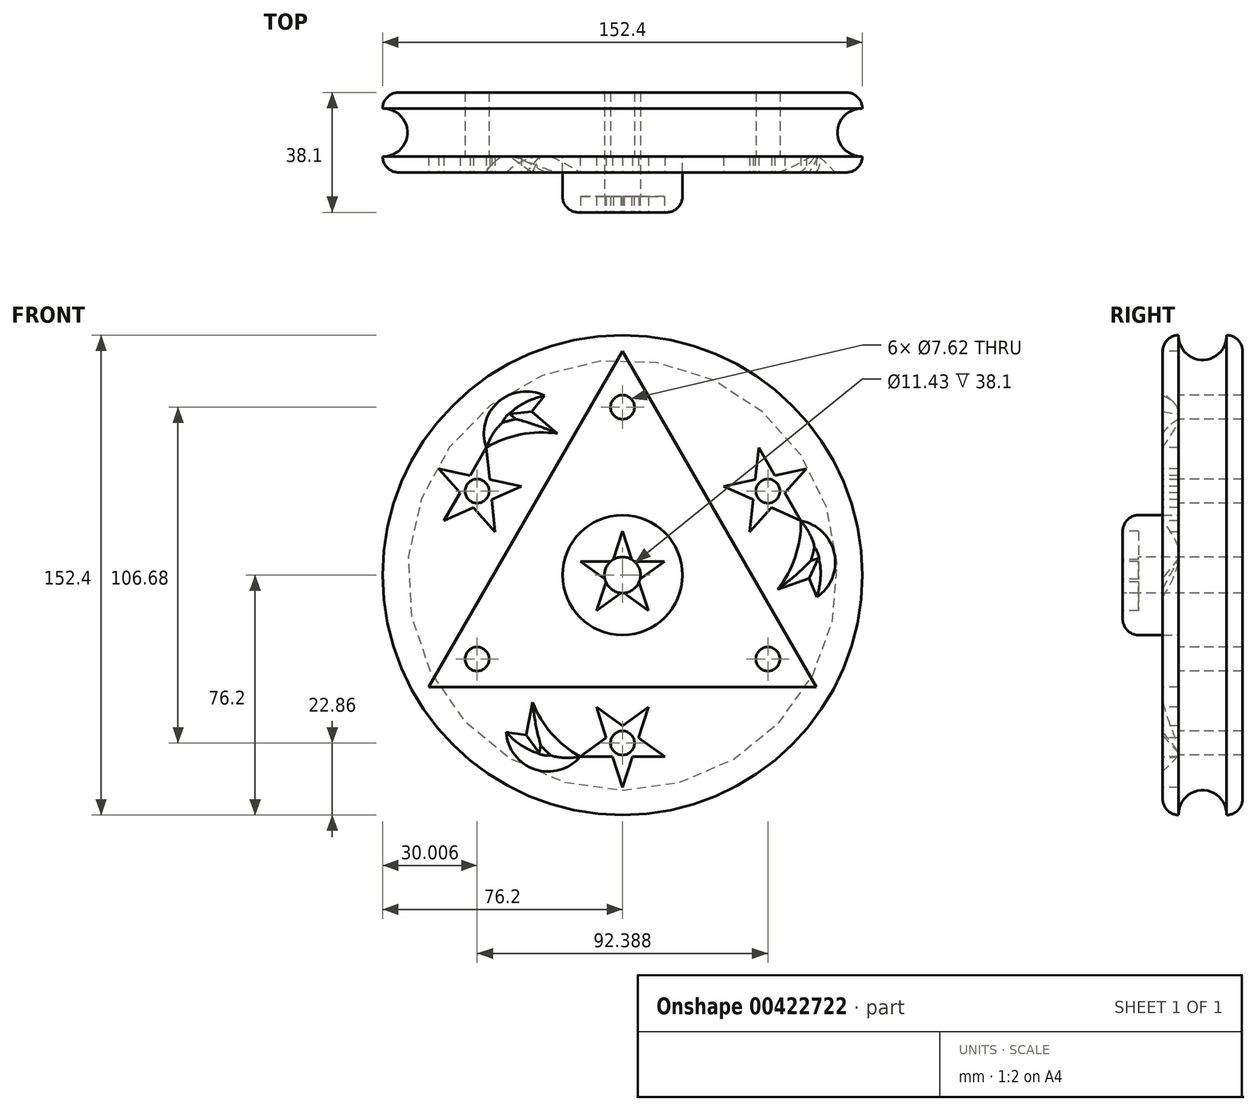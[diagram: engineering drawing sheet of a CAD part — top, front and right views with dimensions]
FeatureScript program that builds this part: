
annotation { "Feature Type Name" : "Feature", "Feature Type Description" : "" }
export const myFeature = defineFeature(function(context is Context, id is Id, definition is map)
    precondition{}
    {
        {
            var Q0;
            Q0=qCreatedBy(makeId("Front.planeOp"),FACE);
            var sketch = newSketch(context, id + "F0", { "sketchPlane" : qUnion([Q0])});
            skCircle(sketch, "E0", {"center": v(0, 0) * mm, "radius": 76.2 * mm});
            skSolve(sketch);
        }
        {
            var Q0;
            Q0=makeQuery(id+"F0.imprint","IMPRINT",FACE,{"disambiguationData":[TD([[makeQuery(id+"F0.imprint","IMPRINT",EDGE,{"derivedFrom":sQuery(id+"F0.wireOp",EDGE,"E0")}),1.0]])]});
            extrude(context, id + "F1", {"entities" : qUnion([Q0]), "depth" : 25.4 * mm});
        }
        {
            var Q0;
            Q0=makeQuery(id+"F1.opExtrude","CAP_FACE",FACE,{"disambiguationData":[OSD([sQuery(id+"F0.wireOp",EDGE,"E0")])],"isStart":false});
            var sketch = newSketch(context, id + "F2", { "sketchPlane" : qUnion([Q0])});
            skCircle(sketch, "E1", {"center": v(0, 0) * mm, "radius": 19.05 * mm});
            skSolve(sketch);
        }
        {
            var Q0;
            Q0=makeQuery(id+"F2.imprint","IMPRINT",FACE,{"disambiguationData":[TD([[makeQuery(id+"F2.imprint","IMPRINT",EDGE,{"derivedFrom":sQuery(id+"F2.wireOp",EDGE,"E1")}),1.0]])]});
            extrude(context, id + "F3", {"entities" : qUnion([Q0]), "operationType" : NewBodyOperationType.ADD, "depth" : 12.7 * mm});
        }
        {
            var Q0;
            Q0=makeQuery(id+"F3.opExtrude","CAP_FACE",FACE,{"disambiguationData":[OSD([sQuery(id+"F2.wireOp",EDGE,"E1")])],"isStart":false});
            var sketch = newSketch(context, id + "F4", { "sketchPlane" : qUnion([Q0])});
            skCircle(sketch, "E2", {"center": v(0, 0) * mm, "radius": 6.35 * mm});
            skSolve(sketch);
        }
        {
            var Q0;
            Q0=sQuery(id+"F4.wireOp",VERTEX,"E2.center");
            var Q1;
            Q1=makeQuery(id+"F1.opExtrude","SWEPT_BODY",BODY,{"disambiguationData":[OSD([sQuery(id+"F0.wireOp",EDGE,"E0")])]});
            hole(context, id + "F5", {"style" : HoleStyle.SIMPLE, "endStyle" : HoleEndStyle.THROUGH, "holeDiameter" : 11.43 * mm, "isTappedThrough" : true, "tappedDepth" : 12.7 * mm, "tapClearance" : 3, "locations" : qUnion([Q0]), "scope" : qUnion([Q1])});
        }
        {
            var Q0;
            Q0=makeQuery(id+"F1.opExtrude","CAP_EDGE",EDGE,{"disambiguationData":[OSD([sQuery(id+"F0.wireOp",EDGE,"E0")])],"isStart":false});
            var Q1;
            Q1=makeQuery(id+"F1.opExtrude","SWEPT_FACE",FACE,{"disambiguationData":[OSD([sQuery(id+"F0.wireOp",EDGE,"E0")])]});
            fillet(context, id + "F6", {"entities" : qUnion([Q0, Q1]), "radius" : 5.08 * mm, "tangentPropagation" : true, "allowEdgeOverflow" : false});
        }
        {
            var Q0;
            Q0=qCreatedBy(makeId("Right.planeOp"),FACE);
            var sketch = newSketch(context, id + "F7", { "sketchPlane" : qUnion([Q0])});
            skCircle(sketch, "E3", {"center": v(-12.7, 75.94) * mm, "radius": 7.61 * mm});
            skPoint(sketch, "E3.first.point", {"position": v(-20.3, 76.36) * mm});
            skPoint(sketch, "E3.second.point", {"position": v(-5.1, 76.06) * mm});
            skPoint(sketch, "E3.third.point", {"position": v(-9.09, 69.24) * mm});
            skSolve(sketch);
        }
        {
            var Q0;
            Q0=makeQuery(id+"F7.imprint","IMPRINT",FACE,{"disambiguationData":[TD([[makeQuery(id+"F7.imprint","IMPRINT",EDGE,{"derivedFrom":sQuery(id+"F7.wireOp",EDGE,"E3")}),1.0]])]});
            var Q1;
            {var subQ0=sQuery(id+"F0.wireOp",EDGE,"E0");Q1=makeQuery(id+"F6.opFillet","BLEND_EDGE",EDGE,{"blendedFrom":[makeQuery(id+"F1.opExtrude","CAP_EDGE",EDGE,{"disambiguationData":[OSD([subQ0])],"isStart":false}),makeQuery(id+"F1.opExtrude","CAP_FACE",FACE,{"disambiguationData":[OSD([subQ0])],"isStart":false})],"blendedInto":[makeQuery(id+"F1.opExtrude","CAP_FACE",FACE,{"disambiguationData":[OSD([subQ0])],"isStart":false})]});}
            revolve(context, id + "F8", {"operationType" : NewBodyOperationType.REMOVE, "entities" : qUnion([Q0]), "axis" : qUnion([Q1]), "revolveType" : RevolveType.FULL, "oppositeDirection" : true});
        }
        {
            var Q0;
            Q0=makeQuery(id+"F1.opExtrude","CAP_FACE",FACE,{"disambiguationData":[OSD([sQuery(id+"F0.wireOp",EDGE,"E0")])],"isStart":false});
            var sketch = newSketch(context, id + "F9", { "sketchPlane" : qUnion([Q0])});
            skCircle(sketch, "E4.cCircle", {"center": v(0, 0) * mm, "radius": 71.12 * mm, "construction": true});
            skLineSegment(sketch, "E4.0", {"start": v(0, 71.12) * mm, "end": v(61.6, -35.56) * mm});
            skLineSegment(sketch, "E4.1", {"start": v(61.6, -35.56) * mm, "end": v(-61.6, -35.56) * mm});
            skLineSegment(sketch, "E4.2", {"start": v(-61.6, -35.56) * mm, "end": v(0, 71.12) * mm});
            skSolve(sketch);
        }
        {
            var Q0;
            Q0=makeQuery(id+"F9.imprint","IMPRINT",FACE,{"disambiguationData":[TD([[makeQuery(id+"F9.imprint","IMPRINT",EDGE,{"derivedFrom":sQuery(id+"F9.wireOp",EDGE,"E4.0")}),-1.0]])]});
            extrude(context, id + "F10", {"entities" : qUnion([Q0]), "operationType" : NewBodyOperationType.REMOVE, "oppositeDirection" : true, "depth" : 5.08 * mm, "offsetDistance" : 25.4 * mm});
        }
        {
            var Q0;
            Q0=makeQuery(id+"F10.boolean.opBoolean","SPLIT",FACE,{"disambiguationData":[OD(2.0)],"derivedFrom":makeQuery(id+"F1.opExtrude","CAP_FACE",FACE,{"disambiguationData":[OSD([sQuery(id+"F0.wireOp",EDGE,"E0")])],"isStart":false})});
            var sketch = newSketch(context, id + "F11", { "sketchPlane" : qUnion([Q0])});
            skCircle(sketch, "E5", {"center": v(-46.2, 26.67) * mm, "radius": 2.54 * mm});
            skCircle(sketch, "E6", {"center": v(46.2, 26.67) * mm, "radius": 2.54 * mm});
            skCircle(sketch, "E7", {"center": v(0, -53.34) * mm, "radius": 2.54 * mm});
            skSolve(sketch);
        }
        {
            var Q0;
            Q0=sQuery(id+"F11.wireOp",VERTEX,"E5.center");
            var Q1;
            Q1=sQuery(id+"F11.wireOp",VERTEX,"E6.center");
            var Q2;
            Q2=sQuery(id+"F11.wireOp",VERTEX,"E7.center");
            var Q3;
            Q3=makeQuery(id+"F1.opExtrude","SWEPT_BODY",BODY,{"disambiguationData":[OSD([sQuery(id+"F0.wireOp",EDGE,"E0")])]});
            hole(context, id + "F12", {"style" : HoleStyle.SIMPLE, "endStyle" : HoleEndStyle.THROUGH, "holeDiameter" : 7.62 * mm, "isTappedThrough" : true, "tappedDepth" : 12.7 * mm, "tapClearance" : 3, "locations" : qUnion([Q0, Q1, Q2]), "scope" : qUnion([Q3])});
        }
        {
            var Q0;
            Q0=makeQuery(id+"F3.opExtrude","CAP_EDGE",EDGE,{"disambiguationData":[OSD([sQuery(id+"F2.wireOp",EDGE,"E1")])],"isStart":false});
            fillet(context, id + "F13", {"entities" : qUnion([Q0]), "radius" : 5.08 * mm, "tangentPropagation" : true, "allowEdgeOverflow" : false});
        }
        {
            var Q0;
            Q0=makeQuery(id+"F10.boolean.opBoolean","SPLIT",FACE,{"disambiguationData":[OD(2.0)],"derivedFrom":makeQuery(id+"F1.opExtrude","CAP_FACE",FACE,{"disambiguationData":[OSD([sQuery(id+"F0.wireOp",EDGE,"E0")])],"isStart":false})});
            var sketch = newSketch(context, id + "F14", { "sketchPlane" : qUnion([Q0])});
            skPoint(sketch, "E8.0.midPoint", {"position": v(-36.3, 20.95) * mm});
            skPoint(sketch, "E9.0.midPoint", {"position": v(0, -41.91) * mm});
            skLineSegment(sketch, "E10", {"start": v(-56.7, 17.22) * mm, "end": v(-32.14, 28.15) * mm});
            skLineSegment(sketch, "E11", {"start": v(-58.43, 33.73) * mm, "end": v(-40.45, 13.76) * mm});
            skLineSegment(sketch, "E12", {"start": v(-56.7, 17.22) * mm, "end": v(-43.26, 40.49) * mm});
            skLineSegment(sketch, "E13", {"start": v(-40.45, 13.76) * mm, "end": v(-43.26, 40.49) * mm});
            skLineSegment(sketch, "E14", {"start": v(-32.14, 28.15) * mm, "end": v(-58.43, 33.73) * mm});
            skLineSegment(sketch, "E15", {"start": v(40.45, 13.76) * mm, "end": v(58.43, 33.73) * mm});
            skLineSegment(sketch, "E16", {"start": v(58.43, 33.73) * mm, "end": v(32.14, 28.15) * mm});
            skLineSegment(sketch, "E17", {"start": v(32.14, 28.15) * mm, "end": v(56.7, 17.22) * mm});
            skLineSegment(sketch, "E18", {"start": v(56.7, 17.22) * mm, "end": v(43.26, 40.49) * mm});
            skLineSegment(sketch, "E19", {"start": v(40.45, 13.76) * mm, "end": v(43.26, 40.49) * mm});
            skLineSegment(sketch, "E20", {"start": v(13.44, -57.7) * mm, "end": v(-8.3, -41.91) * mm});
            skLineSegment(sketch, "E21", {"start": v(-8.3, -41.91) * mm, "end": v(0, -67.47) * mm});
            skLineSegment(sketch, "E22", {"start": v(0, -67.47) * mm, "end": v(8.3, -41.91) * mm});
            skLineSegment(sketch, "E23", {"start": v(8.3, -41.91) * mm, "end": v(-13.44, -57.7) * mm});
            skLineSegment(sketch, "E24", {"start": v(-13.44, -57.7) * mm, "end": v(13.44, -57.7) * mm});
            skSolve(sketch);
        }
        {
            var Q0;
            Q0 = qSketchRegion(id + "F14", true);
            extrude(context, id + "F15", {"entities" : qUnion([Q0]), "operationType" : NewBodyOperationType.REMOVE, "oppositeDirection" : true, "depth" : 5.08 * mm, "offsetDistance" : 25.4 * mm});
        }
        {
            var Q0;
            Q0=makeQuery(id+"F3.opExtrude","CAP_FACE",FACE,{"disambiguationData":[OSD([sQuery(id+"F2.wireOp",EDGE,"E1")])],"isStart":false});
            var sketch = newSketch(context, id + "F16", { "sketchPlane" : qUnion([Q0])});
            skCircle(sketch, "E25.cCircle", {"center": v(0, 0) * mm, "radius": 13.97 * mm, "construction": true});
            skLineSegment(sketch, "E26", {"start": v(-8.21, -11.3) * mm, "end": v(0, 13.97) * mm});
            skLineSegment(sketch, "E27", {"start": v(0, 13.97) * mm, "end": v(8.21, -11.3) * mm});
            skLineSegment(sketch, "E28", {"start": v(8.21, -11.3) * mm, "end": v(-13.29, 4.32) * mm});
            skLineSegment(sketch, "E29", {"start": v(-13.29, 4.32) * mm, "end": v(13.29, 4.32) * mm});
            skLineSegment(sketch, "E30", {"start": v(13.29, 4.32) * mm, "end": v(-8.21, -11.3) * mm});
            skSolve(sketch);
        }
        {
            var Q0;
            Q0 = qSketchRegion(id + "F16", true);
            extrude(context, id + "F17", {"entities" : qUnion([Q0]), "operationType" : NewBodyOperationType.REMOVE, "oppositeDirection" : true, "depth" : 5.08 * mm, "offsetDistance" : 25.4 * mm});
        }
        {
            var Q0;
            Q0=makeQuery(id+"F10.boolean.opBoolean","SPLIT",FACE,{"disambiguationData":[OD(2.0)],"derivedFrom":makeQuery(id+"F1.opExtrude","CAP_FACE",FACE,{"disambiguationData":[OSD([sQuery(id+"F0.wireOp",EDGE,"E0")])],"isStart":false})});
            var sketch = newSketch(context, id + "F18", { "sketchPlane" : qUnion([Q0])});
            skArc(sketch, "E31", {"start": v(-24.76, 56.96) * mm, "mid": v(-39.55, 54.94) * mm, "end": v(-43.26, 40.5) * mm});
            skArc(sketch, "E32", {"start": v(-20.73, 44.96) * mm, "mid": v(-32.38, 44.66) * mm, "end": v(-43.26, 40.5) * mm});
            skLineSegment(sketch, "E33", {"start": v(-24.76, 56.96) * mm, "end": v(-28.77, 51.87) * mm});
            skLineSegment(sketch, "E34", {"start": v(-28.77, 51.87) * mm, "end": v(-20.73, 44.96) * mm});
            skArc(sketch, "E35", {"start": v(-28.77, 51.87) * mm, "mid": v(-39.16, 50.19) * mm, "end": v(-43.26, 40.5) * mm});
            skArc(sketch, "E36.1.0", {"start": v(-36.95, -49.92) * mm, "mid": v(-27.8, -61.72) * mm, "end": v(-13.44, -57.7) * mm});
            skArc(sketch, "E36.1.1", {"start": v(-28.57, -40.44) * mm, "mid": v(-22.49, -50.37) * mm, "end": v(-13.44, -57.7) * mm});
            skLineSegment(sketch, "E36.1.2", {"start": v(-30.54, -50.85) * mm, "end": v(-28.57, -40.44) * mm});
            skArc(sketch, "E36.1.3", {"start": v(-30.54, -50.85) * mm, "mid": v(-23.88, -59) * mm, "end": v(-13.44, -57.7) * mm});
            skLineSegment(sketch, "E36.1.4", {"start": v(-36.95, -49.92) * mm, "end": v(-30.54, -50.85) * mm});
            skArc(sketch, "E36.2.0", {"start": v(61.7, -7.04) * mm, "mid": v(67.35, 6.78) * mm, "end": v(56.7, 17.22) * mm});
            skArc(sketch, "E36.2.1", {"start": v(49.3, -4.52) * mm, "mid": v(54.87, 5.71) * mm, "end": v(56.7, 17.22) * mm});
            skLineSegment(sketch, "E36.2.2", {"start": v(59.3, -1.02) * mm, "end": v(49.3, -4.52) * mm});
            skArc(sketch, "E36.2.3", {"start": v(59.3, -1.02) * mm, "mid": v(63.04, 8.82) * mm, "end": v(56.7, 17.22) * mm});
            skLineSegment(sketch, "E36.2.4", {"start": v(61.7, -7.04) * mm, "end": v(59.3, -1.02) * mm});
            skPoint(sketch, "E36.center", {"position": v(0, 0) * mm});
            skSolve(sketch);
        }
        {
            var Q0;
            Q0 = qSketchRegion(id + "F18", true);
            extrude(context, id + "F19", {"entities" : qUnion([Q0]), "operationType" : NewBodyOperationType.REMOVE, "oppositeDirection" : true, "depth" : 5.08 * mm, "offsetDistance" : 25.4 * mm});
        }
        {
            var Q0;
            Q0=makeQuery(id+"F19.boolean.opBoolean","COPY",FACE,{"derivedFrom":makeQuery(id+"F19.opExtrude","CAP_FACE",FACE,{"disambiguationData":[OSD([sQuery(id+"F18.wireOp",EDGE,"E31"),sQuery(id+"F18.wireOp",EDGE,"E32"),sQuery(id+"F18.wireOp",EDGE,"E33"),sQuery(id+"F18.wireOp",EDGE,"E34")])],"isStart":false})});
            var Q1;
            Q1=makeQuery(id+"F19.boolean.opBoolean","COPY",FACE,{"derivedFrom":makeQuery(id+"F19.opExtrude","CAP_FACE",FACE,{"disambiguationData":[OSD([sQuery(id+"F18.wireOp",EDGE,"E36.2.0"),sQuery(id+"F18.wireOp",EDGE,"E36.2.1"),sQuery(id+"F18.wireOp",EDGE,"E36.2.2"),sQuery(id+"F18.wireOp",EDGE,"E36.2.4")])],"isStart":false})});
            var Q2;
            Q2=makeQuery(id+"F19.boolean.opBoolean","COPY",FACE,{"derivedFrom":makeQuery(id+"F19.opExtrude","CAP_FACE",FACE,{"disambiguationData":[OSD([sQuery(id+"F18.wireOp",EDGE,"E36.1.0"),sQuery(id+"F18.wireOp",EDGE,"E36.1.1"),sQuery(id+"F18.wireOp",EDGE,"E36.1.2"),sQuery(id+"F18.wireOp",EDGE,"E36.1.4")])],"isStart":false})});
            chamfer(context, id + "F20", {"entities" : qUnion([Q0, Q1, Q2]), "width" : 5.08 * mm, "tangentPropagation" : true});
        }
        {
            var Q0;
            Q0=makeQuery(id+"F10.boolean.opBoolean","COPY",FACE,{"derivedFrom":makeQuery(id+"F10.opExtrude","CAP_FACE",FACE,{"disambiguationData":[OSD([sQuery(id+"F2.wireOp",EDGE,"E1"),sQuery(id+"F9.wireOp",EDGE,"E4.0"),sQuery(id+"F9.wireOp",EDGE,"E4.1"),sQuery(id+"F9.wireOp",EDGE,"E4.2")])],"isStart":false})});
            var sketch = newSketch(context, id + "F21", { "sketchPlane" : qUnion([Q0])});
            skCircle(sketch, "E37", {"center": v(0, 53.34) * mm, "radius": 3.81 * mm});
            skPoint(sketch, "E38.center", {"position": v(0, -1.9) * mm});
            skPoint(sketch, "E39", {"position": v(0, -53.34) * mm});
            skCircle(sketch, "E40.1.0", {"center": v(-46.2, -26.67) * mm, "radius": 3.81 * mm});
            skCircle(sketch, "E40.2.0", {"center": v(46.2, -26.67) * mm, "radius": 3.81 * mm});
            skPoint(sketch, "E40.center", {"position": v(0, 0) * mm});
            skSolve(sketch);
        }
        {
            var Q0;
            Q0=sQuery(id+"F21.wireOp",VERTEX,"E40.1.0.center");
            var Q1;
            Q1=sQuery(id+"F21.wireOp",VERTEX,"E37.center");
            var Q2;
            Q2=sQuery(id+"F21.wireOp",VERTEX,"E40.2.0.center");
            var Q3;
            Q3=makeQuery(id+"F1.opExtrude","SWEPT_BODY",BODY,{"disambiguationData":[OSD([sQuery(id+"F0.wireOp",EDGE,"E0")])]});
            hole(context, id + "F22", {"style" : HoleStyle.SIMPLE, "endStyle" : HoleEndStyle.THROUGH, "holeDiameter" : 7.62 * mm, "majorDiameter" : 6.35 * mm, "isTappedThrough" : true, "tappedDepth" : 12.7 * mm, "tapClearance" : 3, "locations" : qUnion([Q0, Q1, Q2]), "scope" : qUnion([Q3])});
        }
    });
